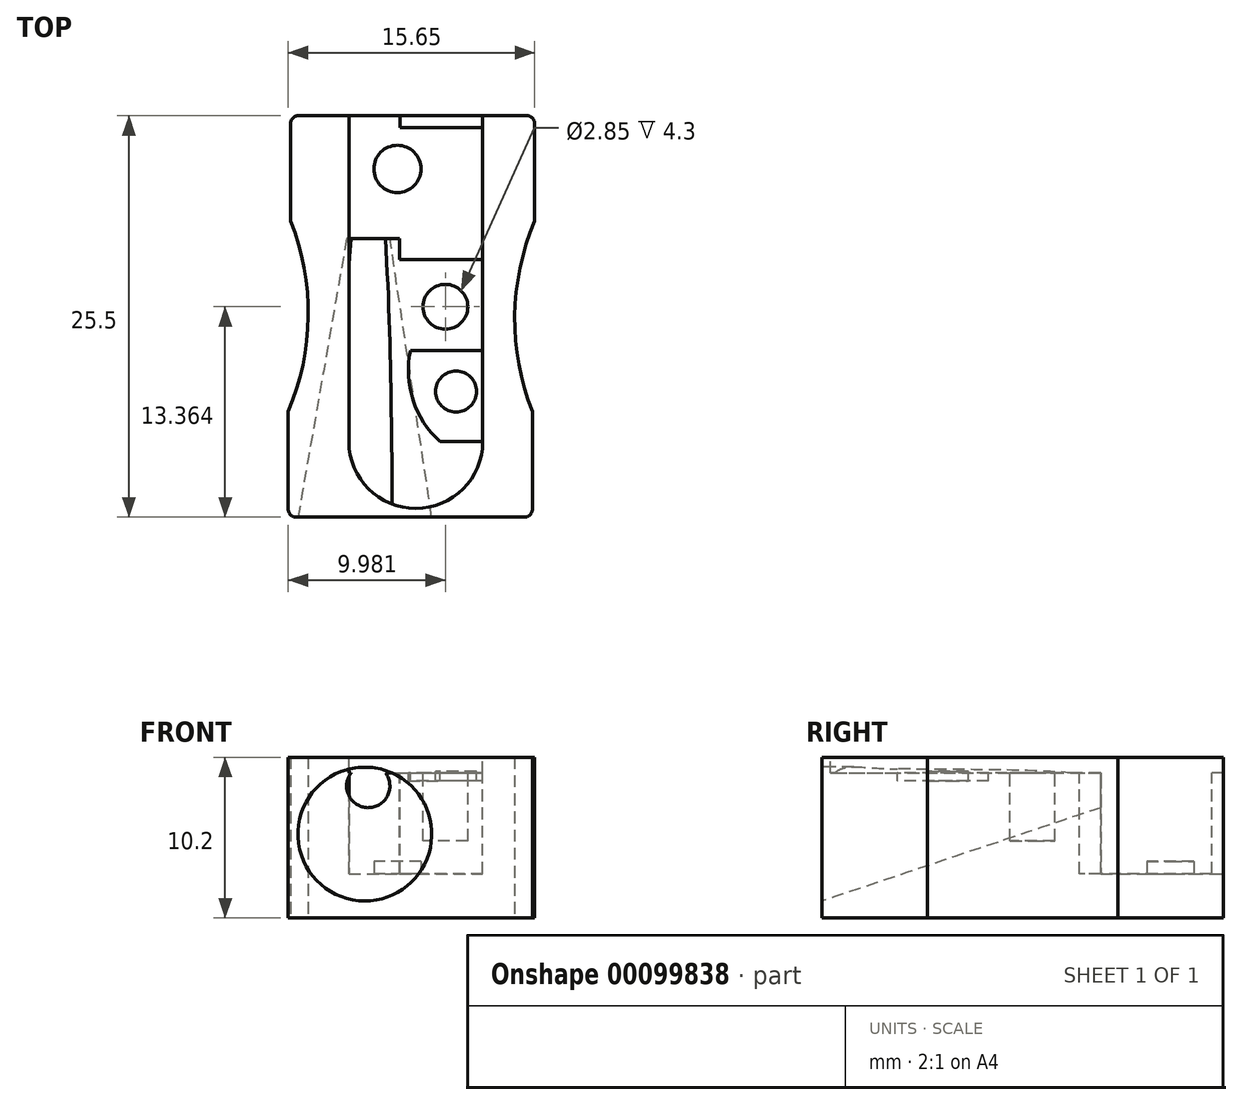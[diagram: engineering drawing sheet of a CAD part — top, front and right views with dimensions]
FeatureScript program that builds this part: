
annotation { "Feature Type Name" : "Feature", "Feature Type Description" : "" }
export const myFeature = defineFeature(function(context is Context, id is Id, definition is map)
    precondition{}
    {
        {
            var Q0;
            Q0=qCreatedBy(makeId("Top.planeOp"),FACE);
            var sketch = newSketch(context, id + "F0", { "sketchPlane" : qUnion([Q0])});
            skLineSegment(sketch, "E0", {"start": v(-7.6, 25.5) * mm, "end": v(7.9, 25.5) * mm});
            skLineSegment(sketch, "E1", {"start": v(7.75, 0) * mm, "end": v(-7.75, 0) * mm});
            skLineSegment(sketch, "E2", {"start": v(7.9, 25.5) * mm, "end": v(7.9, 18.8) * mm});
            skLineSegment(sketch, "E3", {"start": v(7.75, 0) * mm, "end": v(7.75, 6.7) * mm});
            skArc(sketch, "E4", {"start": v(7.9, 18.8) * mm, "mid": v(6.63, 12.76) * mm, "end": v(7.75, 6.7) * mm});
            skLineSegment(sketch, "E5", {"start": v(-7.6, 25.5) * mm, "end": v(-7.6, 18.8) * mm});
            skLineSegment(sketch, "E6", {"start": v(-7.75, 0) * mm, "end": v(-7.75, 6.7) * mm});
            skArc(sketch, "E7", {"start": v(-7.75, 6.7) * mm, "mid": v(-6.48, 12.74) * mm, "end": v(-7.6, 18.8) * mm});
            skSolve(sketch);
        }
        {
            var Q0;
            Q0 = qSketchRegion(id + "F0", true);
            extrude(context, id + "F1", {"entities" : qUnion([Q0]), "depth" : 10.2 * mm});
        }
        {
            var Q0;
            Q0=makeQuery(id+"F1.opExtrude","CAP_FACE",FACE,{"disambiguationData":[OSD([sQuery(id+"F0.wireOp",EDGE,"gVELieU4-cspG-5G9I-3kCS-hAkd85Fw9fWJ"),sQuery(id+"F0.wireOp",EDGE,"E0"),sQuery(id+"F0.wireOp",EDGE,"jVQGG9Pi-WTZj-yuHM-hF9S-3tLnvCRLDn7S"),sQuery(id+"F0.wireOp",EDGE,"E1")])],"isStart":false});
            var sketch = newSketch(context, id + "F2", { "sketchPlane" : qUnion([Q0])});
            skLineSegment(sketch, "E8", {"start": v(4.6, 25.5) * mm, "end": v(4.6, 4.8) * mm});
            skLineSegment(sketch, "E9", {"start": v(-3.9, 4.8) * mm, "end": v(-3.9, 25.5) * mm});
            skArc(sketch, "E10", {"start": v(-3.9, 4.8) * mm, "mid": v(0.35, 0.55) * mm, "end": v(4.6, 4.8) * mm});
            skSolve(sketch);
        }
        {
            var Q0;
            {var subQ0=sQuery(id+"F2.wireOp",EDGE,"E8");Q0=makeQuery(id+"F2.imprint","IMPRINT",FACE,{"disambiguationData":[TD([[makeQuery(id+"F2.imprint","IMPRINT",EDGE,{"derivedFrom":subQ0}),-1.0]])]});}
            extrude(context, id + "F3", {"entities" : qUnion([Q0]), "operationType" : NewBodyOperationType.REMOVE, "oppositeDirection" : true, "depth" : 1 * mm});
        }
        {
            var Q0;
            Q0=qCreatedBy(makeId("Front.planeOp"),FACE);
            var Q1;
            Q1 = qBodyType(qCreatedBy(id + "F5" ,EDGE), BodyType.WIRE);
            cPlane(context, id + "F4", {"entities" : qUnion([Q0, Q1]), "cplaneType" : CPlaneType.OFFSET, "offset" : 17.7 * mm, "oppositeDirection" : true, "width" : 150 * mm, "height" : 150 * mm});
        }
        {
            var Q0;
            Q0=makeQuery(id+"F1.opExtrude","SWEPT_FACE",FACE,{"disambiguationData":[OSD([sQuery(id+"F0.wireOp",EDGE,"E1")])]});
            var sketch = newSketch(context, id + "F5", { "sketchPlane" : qUnion([Q0])});
            skCircle(sketch, "E11", {"center": v(-2.89, 5.32) * mm, "radius": 4.25 * mm});
            skSolve(sketch);
        }
        {
            var Q0;
            Q0=qCreatedBy(id+"F4.planeOp",FACE);
            var sketch = newSketch(context, id + "F6", { "sketchPlane" : qUnion([Q0])});
            skCircle(sketch, "E12", {"center": v(-2.67, 8.37) * mm, "radius": 1.37 * mm});
            skSolve(sketch);
        }
        {
            var Q1;
            Q1=makeQuery(id+"F5.imprint","IMPRINT",FACE,{"disambiguationData":[TD([[makeQuery(id+"F5.imprint","IMPRINT",EDGE,{"derivedFrom":sQuery(id+"F5.wireOp",EDGE,"E11")}),1.0]])]});
            var Q2;
            Q2=makeQuery(id+"F6.imprint","IMPRINT",FACE,{"disambiguationData":[TD([[makeQuery(id+"F6.imprint","IMPRINT",EDGE,{"derivedFrom":sQuery(id+"F6.wireOp",EDGE,"E12")}),1.0]])]});
            loft(context, id + "F7", {"operationType" : NewBodyOperationType.REMOVE, "sheetProfilesArray" : [{ "sheetProfileEntities" : qUnion([Q1]) }, { "sheetProfileEntities" : qUnion([Q2]) }]});
        }
        {
            var Q0;
            Q0=makeQuery(id+"F1.opExtrude","SWEPT_FACE",FACE,{"disambiguationData":[OSD([sQuery(id+"F0.wireOp",EDGE,"E0")])]});
            var sketch = newSketch(context, id + "F8", { "sketchPlane" : qUnion([Q0])});
            skLineSegment(sketch, "E13", {"start": v(3.9, 9.2) * mm, "end": v(3.9, 2.8) * mm});
            skLineSegment(sketch, "E14", {"start": v(3.9, 2.8) * mm, "end": v(0.65, 2.8) * mm});
            skLineSegment(sketch, "E15", {"start": v(0.65, 2.8) * mm, "end": v(0.65, 9.2) * mm});
            skLineSegment(sketch, "E16", {"start": v(0.65, 9.2) * mm, "end": v(3.9, 9.2) * mm});
            skSolve(sketch);
        }
        {
            var Q0;
            Q0 = qSketchRegion(id + "F8", true);
            extrude(context, id + "F9", {"entities" : qUnion([Q0]), "operationType" : NewBodyOperationType.REMOVE, "oppositeDirection" : true, "depth" : 7.8 * mm});
        }
        {
            var Q0;
            Q0=makeQuery(id+"F1.opExtrude","CAP_FACE",FACE,{"disambiguationData":[OSD([sQuery(id+"F0.wireOp",EDGE,"E0"),sQuery(id+"F0.wireOp",EDGE,"E1"),sQuery(id+"F0.wireOp",EDGE,"E2"),sQuery(id+"F0.wireOp",EDGE,"E3"),sQuery(id+"F0.wireOp",EDGE,"E4"),sQuery(id+"F0.wireOp",EDGE,"E5"),sQuery(id+"F0.wireOp",EDGE,"E6"),sQuery(id+"F0.wireOp",EDGE,"E7")])],"isStart":false});
            var sketch = newSketch(context, id + "F10", { "sketchPlane" : qUnion([Q0])});
            skLineSegment(sketch, "E17", {"start": v(-0.68, 18.05) * mm, "end": v(-0.68, 16.35) * mm});
            skLineSegment(sketch, "E18", {"start": v(-0.68, 16.35) * mm, "end": v(4.6, 16.35) * mm});
            skPoint(sketch, "E18.endSnap0", {"position": v(4.6, 15.15) * mm});
            skLineSegment(sketch, "E19", {"start": v(4.6, 16.35) * mm, "end": v(4.6, 24.75) * mm});
            skLineSegment(sketch, "E20", {"start": v(4.6, 24.75) * mm, "end": v(-0.68, 24.75) * mm});
            skLineSegment(sketch, "E21", {"start": v(-0.68, 24.75) * mm, "end": v(-0.68, 16.35) * mm});
            skSolve(sketch);
        }
        {
            var Q0;
            {var subQ0=sQuery(id+"F10.wireOp",EDGE,"E18");Q0=makeQuery(id+"F10.imprint","IMPRINT",FACE,{"disambiguationData":[TD([[makeQuery(id+"F10.imprint","IMPRINT",EDGE,{"derivedFrom":subQ0}),1.0]])]});}
            extrude(context, id + "F11", {"entities" : qUnion([Q0]), "operationType" : NewBodyOperationType.REMOVE, "oppositeDirection" : true, "depth" : 7.4 * mm});
        }
        {
            var Q0;
            {var subQ3=sQuery(id+"F2.wireOp",EDGE,"E10");var subQ4=makeQuery(id+"F3.boolean.opBoolean","COPY",FACE,{"derivedFrom":makeQuery(id+"F3.opExtrude","SWEPT_FACE",FACE,{"disambiguationData":[OSD([subQ3])]})});var subQ5=sQuery(id+"F2.wireOp",EDGE,"E8");var subQ7=sQuery(id+"F0.wireOp",EDGE,"E0");Q0=makeQuery(id+"F11.boolean.opBoolean","SPLIT",FACE,{"disambiguationData":[TD([subQ4])],"derivedFrom":makeQuery(id+"F9.boolean.opBoolean","SPLIT",FACE,{"disambiguationData":[TD([makeQuery(id+"F1.opExtrude","SWEPT_FACE",FACE,{"disambiguationData":[OSD([subQ7])]})])],"derivedFrom":makeQuery(id+"F3.boolean.opBoolean","COPY",FACE,{"derivedFrom":makeQuery(id+"F3.opExtrude","CAP_FACE",FACE,{"disambiguationData":[OSD([subQ7,subQ5,sQuery(id+"F2.wireOp",EDGE,"E9"),subQ3])],"isStart":false})})})});}
            var sketch = newSketch(context, id + "F12", { "sketchPlane" : qUnion([Q0])});
            skLineSegment(sketch, "E22", {"start": v(4.6, 10.57) * mm, "end": v(0, 10.57) * mm});
            skLineSegment(sketch, "E23", {"start": v(4.6, 4.8) * mm, "end": v(1.88, 4.8) * mm});
            skArc(sketch, "E24", {"start": v(0, 10.57) * mm, "mid": v(0.18, 7.44) * mm, "end": v(1.88, 4.8) * mm});
            skCircle(sketch, "E25", {"center": v(2.23, 13.36) * mm, "radius": 1.43 * mm});
            skCircle(sketch, "E26", {"center": v(2.9, 7.98) * mm, "radius": 1.3 * mm});
            skSolve(sketch);
        }
        {
            var Q0;
            {var subQ0=sQuery(id+"F12.wireOp",EDGE,"E22");Q0=makeQuery(id+"F12.imprint","IMPRINT",FACE,{"disambiguationData":[TD([[makeQuery(id+"F12.imprint","IMPRINT",EDGE,{"derivedFrom":subQ0}),1.0]])]});}
            extrude(context, id + "F13", {"entities" : qUnion([Q0]), "operationType" : NewBodyOperationType.REMOVE, "oppositeDirection" : true, "depth" : 0.5 * mm});
        }
        {
            var Q0;
            Q0=makeQuery(id+"F12.imprint","IMPRINT",FACE,{"disambiguationData":[TD([[makeQuery(id+"F12.imprint","IMPRINT",EDGE,{"derivedFrom":sQuery(id+"F12.wireOp",EDGE,"E25")}),1.0]])]});
            extrude(context, id + "F14", {"entities" : qUnion([Q0]), "operationType" : NewBodyOperationType.REMOVE, "oppositeDirection" : true, "depth" : 4.3 * mm});
        }
        {
            var Q0;
            {var subQ3=sQuery(id+"F2.wireOp",EDGE,"E10");var subQ4=makeQuery(id+"F3.boolean.opBoolean","COPY",FACE,{"derivedFrom":makeQuery(id+"F3.opExtrude","SWEPT_FACE",FACE,{"disambiguationData":[OSD([subQ3])]})});var subQ5=sQuery(id+"F2.wireOp",EDGE,"E8");var subQ7=sQuery(id+"F0.wireOp",EDGE,"E0");Q0=makeQuery(id+"F13.boolean.opBoolean","SPLIT",FACE,{"disambiguationData":[TD([makeQuery(id+"F13.opExtrude","SWEPT_FACE",FACE,{"disambiguationData":[OSD([sQuery(id+"F12.wireOp",EDGE,"E26")])]})])],"derivedFrom":makeQuery(id+"F11.boolean.opBoolean","SPLIT",FACE,{"disambiguationData":[TD([subQ4])],"derivedFrom":makeQuery(id+"F9.boolean.opBoolean","SPLIT",FACE,{"disambiguationData":[TD([makeQuery(id+"F1.opExtrude","SWEPT_FACE",FACE,{"disambiguationData":[OSD([subQ7])]})])],"derivedFrom":makeQuery(id+"F3.boolean.opBoolean","COPY",FACE,{"derivedFrom":makeQuery(id+"F3.opExtrude","CAP_FACE",FACE,{"disambiguationData":[OSD([subQ7,subQ5,sQuery(id+"F2.wireOp",EDGE,"E9"),subQ3])],"isStart":false})})})})});}
            var Q1;
            Q1 = qSketchRegion(id + "F16", true);
            extrude(context, id + "F15", {"entities" : qUnion([Q0, Q1]), "operationType" : NewBodyOperationType.ADD, "depth" : 0.1 * mm});
        }
        {
            var Q0;
            Q0=makeQuery(id+"F11.boolean.opBoolean","MERGE",FACE,{"derivedFrom":[makeQuery(id+"F9.boolean.opBoolean","COPY",FACE,{"derivedFrom":makeQuery(id+"F9.opExtrude","SWEPT_FACE",FACE,{"disambiguationData":[OSD([sQuery(id+"F8.wireOp",EDGE,"E14")])]})}),makeQuery(id+"F11.opExtrude","CAP_FACE",FACE,{"disambiguationData":[OSD([sQuery(id+"F10.wireOp",EDGE,"E18"),sQuery(id+"F10.wireOp",EDGE,"E19"),sQuery(id+"F10.wireOp",EDGE,"E20"),sQuery(id+"F10.wireOp",EDGE,"E21")])],"isStart":false})]});
            var sketch = newSketch(context, id + "F16", { "sketchPlane" : qUnion([Q0])});
            skCircle(sketch, "E27", {"center": v(-0.81, 22.12) * mm, "radius": 1.5 * mm});
            skSolve(sketch);
        }
        {
            var Q0;
            Q0 = qSketchRegion(id + "F16", true);
            extrude(context, id + "F17", {"entities" : qUnion([Q0]), "operationType" : NewBodyOperationType.ADD, "depth" : 0.8 * mm});
        }
        {
            var Q0;
            Q0=makeQuery(id+"F1.opExtrude","SWEPT_EDGE",EDGE,{"disambiguationData":[OSD([sQuery(id+"F0.wireOp",EDGE,"E1"),sQuery(id+"F0.wireOp",EDGE,"E3")])]});
            var Q1;
            Q1=makeQuery(id+"F1.opExtrude","SWEPT_EDGE",EDGE,{"disambiguationData":[OSD([sQuery(id+"F0.wireOp",EDGE,"E1"),sQuery(id+"F0.wireOp",EDGE,"E6")])]});
            var Q2;
            Q2=makeQuery(id+"F1.opExtrude","SWEPT_EDGE",EDGE,{"disambiguationData":[OSD([sQuery(id+"F0.wireOp",EDGE,"E0"),sQuery(id+"F0.wireOp",EDGE,"E2")])]});
            var Q3;
            Q3=makeQuery(id+"F1.opExtrude","SWEPT_EDGE",EDGE,{"disambiguationData":[OSD([sQuery(id+"F0.wireOp",EDGE,"E0"),sQuery(id+"F0.wireOp",EDGE,"E5")])]});
            fillet(context, id + "F18", {"entities" : qUnion([Q0, Q1, Q2, Q3]), "radius" : 0.5 * mm, "tangentPropagation" : true, "allowEdgeOverflow" : false});
        }
    });
